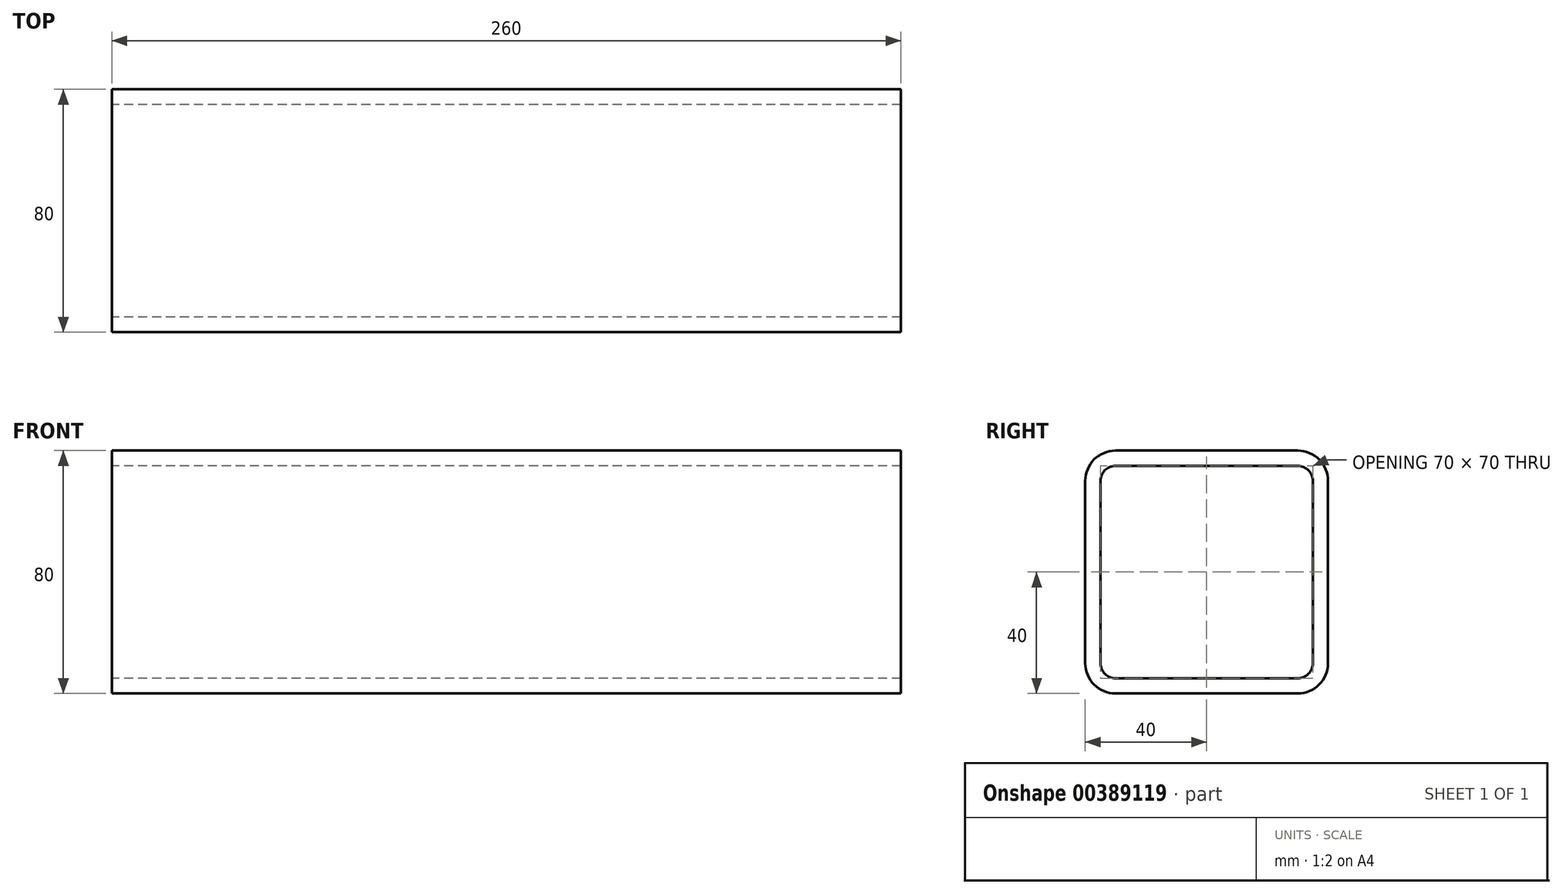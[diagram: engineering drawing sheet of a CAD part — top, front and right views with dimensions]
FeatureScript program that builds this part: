
annotation { "Feature Type Name" : "Feature", "Feature Type Description" : "" }
export const myFeature = defineFeature(function(context is Context, id is Id, definition is map)
    precondition{}
    {
        {
            var Q0;
            Q0=qCreatedBy(makeId("Right.planeOp"),FACE);
            var sketch = newSketch(context, id + "F0", { "sketchPlane" : qUnion([Q0])});
            skLineSegment(sketch, "E0.bottom", {"start": v(30, 40) * mm, "end": v(-30, 40) * mm});
            skLineSegment(sketch, "E0.top", {"start": v(30, -40) * mm, "end": v(-30, -40) * mm});
            skLineSegment(sketch, "E0.left", {"start": v(40, 30) * mm, "end": v(40, -30) * mm});
            skLineSegment(sketch, "E0.right", {"start": v(-40, 30) * mm, "end": v(-40, -30) * mm});
            skPoint(sketch, "E0.middle", {"position": v(0, 0) * mm});
            skPoint(sketch, "E1.visualSharp", {"position": v(-40, 40) * mm});
            skArc(sketch, "E1.filletArc", {"start": v(-30, 40) * mm, "mid": v(-37.07, 37.07) * mm, "end": v(-40, 30) * mm});
            skPoint(sketch, "E2.visualSharp", {"position": v(40, 40) * mm});
            skArc(sketch, "E2.filletArc", {"start": v(40, 30) * mm, "mid": v(37.07, 37.07) * mm, "end": v(30, 40) * mm});
            skPoint(sketch, "E3.visualSharp", {"position": v(40, -40) * mm});
            skArc(sketch, "E3.filletArc", {"start": v(30, -40) * mm, "mid": v(37.07, -37.07) * mm, "end": v(40, -30) * mm});
            skPoint(sketch, "E4.visualSharp", {"position": v(-40, -40) * mm});
            skArc(sketch, "E4.filletArc", {"start": v(-40, -30) * mm, "mid": v(-37.07, -37.07) * mm, "end": v(-30, -40) * mm});
            skArc(sketch, "E5.0", {"start": v(35, 30) * mm, "mid": v(33.54, 33.54) * mm, "end": v(30, 35) * mm});
            skLineSegment(sketch, "E5.1", {"start": v(35, 30) * mm, "end": v(35, -30) * mm});
            skLineSegment(sketch, "E5.2", {"start": v(30, 35) * mm, "end": v(-30, 35) * mm});
            skArc(sketch, "E5.3", {"start": v(30, -35) * mm, "mid": v(33.54, -33.54) * mm, "end": v(35, -30) * mm});
            skArc(sketch, "E5.4", {"start": v(-30, 35) * mm, "mid": v(-33.54, 33.54) * mm, "end": v(-35, 30) * mm});
            skLineSegment(sketch, "E5.5", {"start": v(-35, 30) * mm, "end": v(-35, -30) * mm});
            skArc(sketch, "E5.6", {"start": v(-35, -30) * mm, "mid": v(-33.54, -33.54) * mm, "end": v(-30, -35) * mm});
            skLineSegment(sketch, "E5.7", {"start": v(30, -35) * mm, "end": v(-30, -35) * mm});
            skSolve(sketch);
        }
        {
            var Q0;
            Q0 = qSketchRegion(id + "F0", true);
            extrude(context, id + "F1", {"entities" : qUnion([Q0]), "endBound" : BoundingType.SYMMETRIC, "depth" : 260 * mm});
        }
    });
